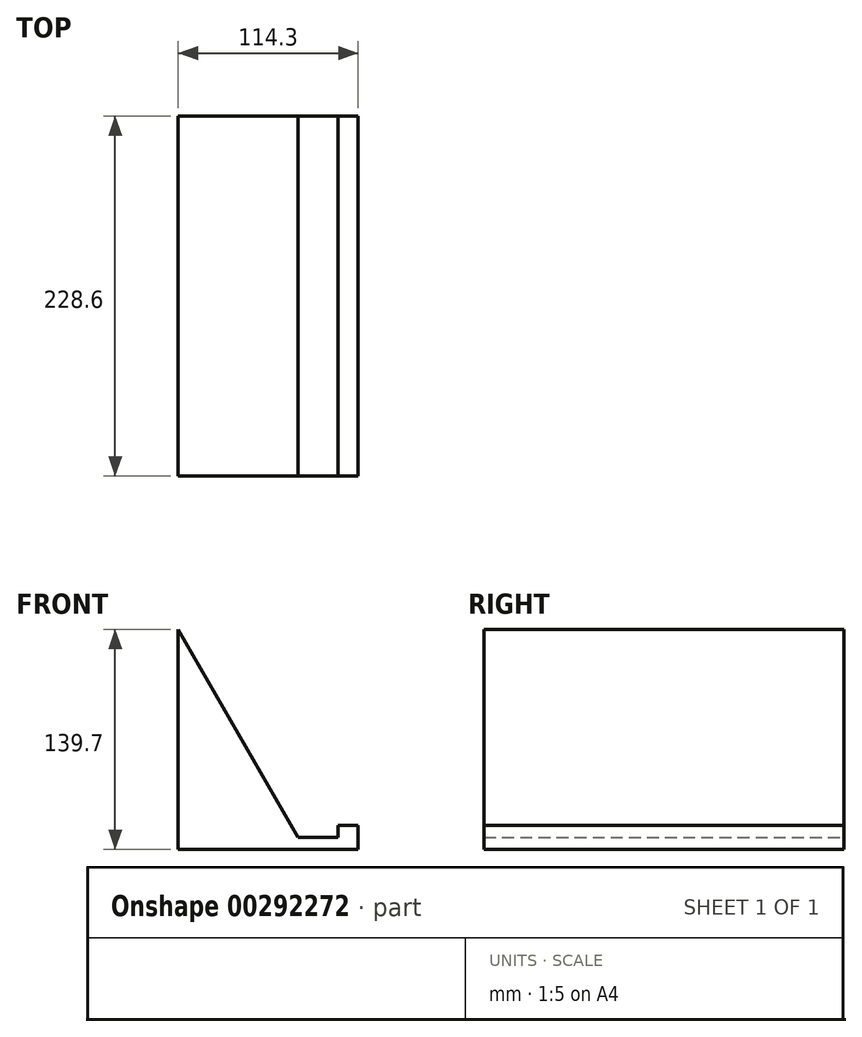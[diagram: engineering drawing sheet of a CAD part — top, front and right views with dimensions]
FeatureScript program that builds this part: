
annotation { "Feature Type Name" : "Feature", "Feature Type Description" : "" }
export const myFeature = defineFeature(function(context is Context, id is Id, definition is map)
    precondition{}
    {
        {
            var Q0;
            Q0=qCreatedBy(makeId("Front.planeOp"),FACE);
            var sketch = newSketch(context, id + "F0", { "sketchPlane" : qUnion([Q0])});
            skLineSegment(sketch, "E0", {"start": v(-114.3, 0) * mm, "end": v(-114.3, 139.7) * mm});
            skLineSegment(sketch, "E1", {"start": v(-114.3, 0) * mm, "end": v(0, 0) * mm});
            skLineSegment(sketch, "E2", {"start": v(0, 0) * mm, "end": v(0, 15.24) * mm});
            skLineSegment(sketch, "E3", {"start": v(0, 15.24) * mm, "end": v(-12.7, 15.24) * mm});
            skLineSegment(sketch, "E4", {"start": v(-12.7, 15.24) * mm, "end": v(-12.7, 7.62) * mm});
            skLineSegment(sketch, "E5", {"start": v(-12.7, 7.62) * mm, "end": v(-38.1, 7.62) * mm});
            skLineSegment(sketch, "E6", {"start": v(-38.1, 7.62) * mm, "end": v(-114.3, 139.7) * mm});
            skSolve(sketch);
        }
        {
            var Q0;
            Q0 = qSketchRegion(id + "F0", true);
            extrude(context, id + "F1", {"entities" : qUnion([Q0]), "depth" : 228.6 * mm});
        }
    });
